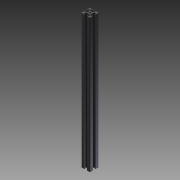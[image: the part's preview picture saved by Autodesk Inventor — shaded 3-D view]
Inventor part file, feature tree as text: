
AUTODESK INVENTOR PART (.ipt)
format: ipt  version: 2014 SP1 (Build 180222100, 222)  size: 176,640 bytes
history: native  units: mm
features: other x7, sketch x2, extrude x1, revolve x1
ambient origin geometry x8: Origin, YZ Plane, XZ Plane, XY Plane, X Axis, Y Axis, Z Axis, Center Point
bodies: Solid1 (feature_tree)
feature tree (11):
  extrude  "Extrusion1"  TaperAngle=360.0deg  [1 undecoded]
  revolve  "Revolution1"  [1 undecoded]
  other  "C1_XY"
  other  "C1_YZ"
  other  "C1_ZX"
  other  "C1_X"
  other  "C1_Y"
  other  "C1_Z"
  other  "C1_Center"
  sketch  "Sketch_1"  dims[d0=311.58mm d1=0.0mm d2=360.0deg]
  sketch  "Sketch_2"
note: 2 required parameter values undecoded (feature->parameter linkage not recoverable at this tier; creation-order binding heuristic only, values carry confidence <= 0.55)
